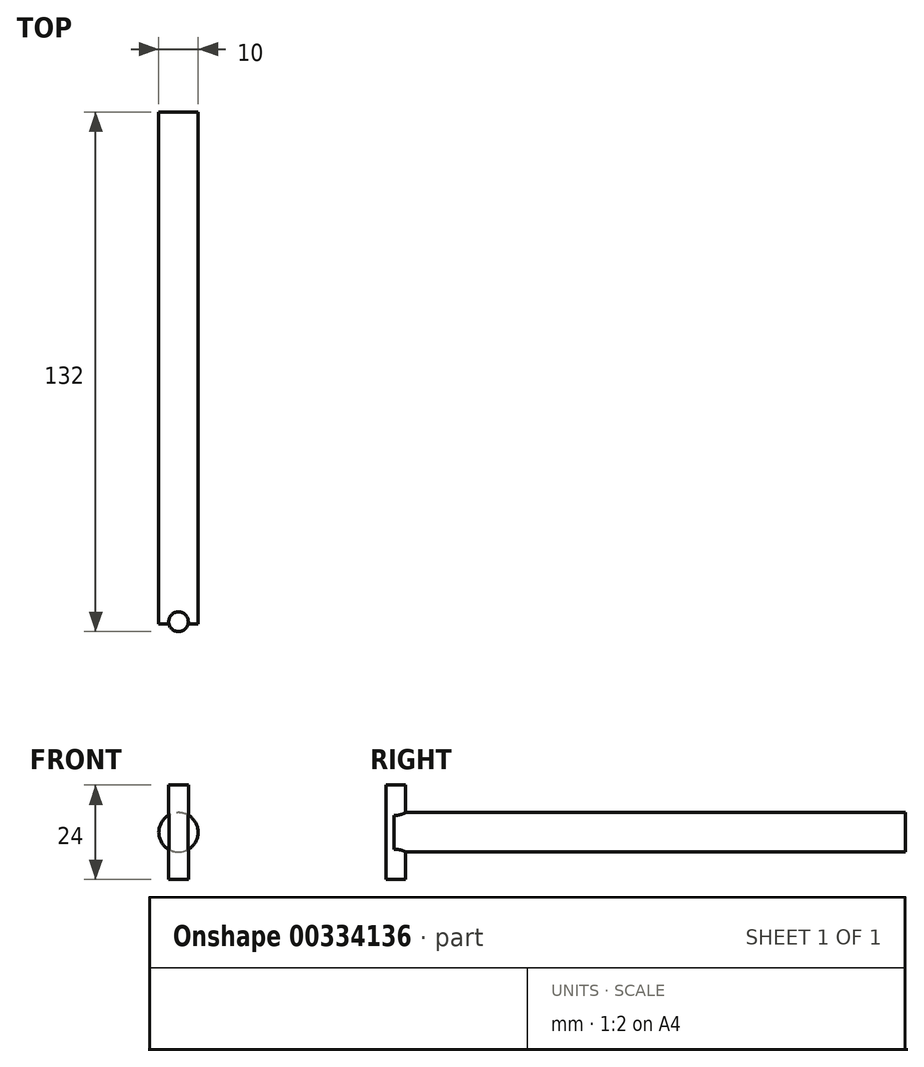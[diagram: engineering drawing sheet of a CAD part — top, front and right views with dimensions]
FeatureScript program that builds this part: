
annotation { "Feature Type Name" : "Feature", "Feature Type Description" : "" }
export const myFeature = defineFeature(function(context is Context, id is Id, definition is map)
    precondition{}
    {
        {
            var Q0;
            Q0=qCreatedBy(makeId("Front.planeOp"),FACE);
            var sketch = newSketch(context, id + "F0", { "sketchPlane" : qUnion([Q0])});
            skCircle(sketch, "E0", {"center": v(0, 0) * mm, "radius": 5 * mm});
            skSolve(sketch);
        }
        {
            var Q0;
            Q0 = qSketchRegion(id + "F0", true);
            extrude(context, id + "F1", {"entities" : qUnion([Q0]), "depth" : 130 * mm});
        }
        {
            var Q0;
            Q0=qCreatedBy(makeId("Top.planeOp"),FACE);
            var sketch = newSketch(context, id + "F2", { "sketchPlane" : qUnion([Q0])});
            skCircle(sketch, "E1", {"center": v(0, -129.5) * mm, "radius": 2.5 * mm});
            skSolve(sketch);
        }
        {
            var Q0;
            Q0 = qSketchRegion(id + "F2", true);
            extrude(context, id + "F3", {"entities" : qUnion([Q0]), "operationType" : NewBodyOperationType.ADD, "depth" : 24 * mm, "symmetric" : true});
        }
    });
